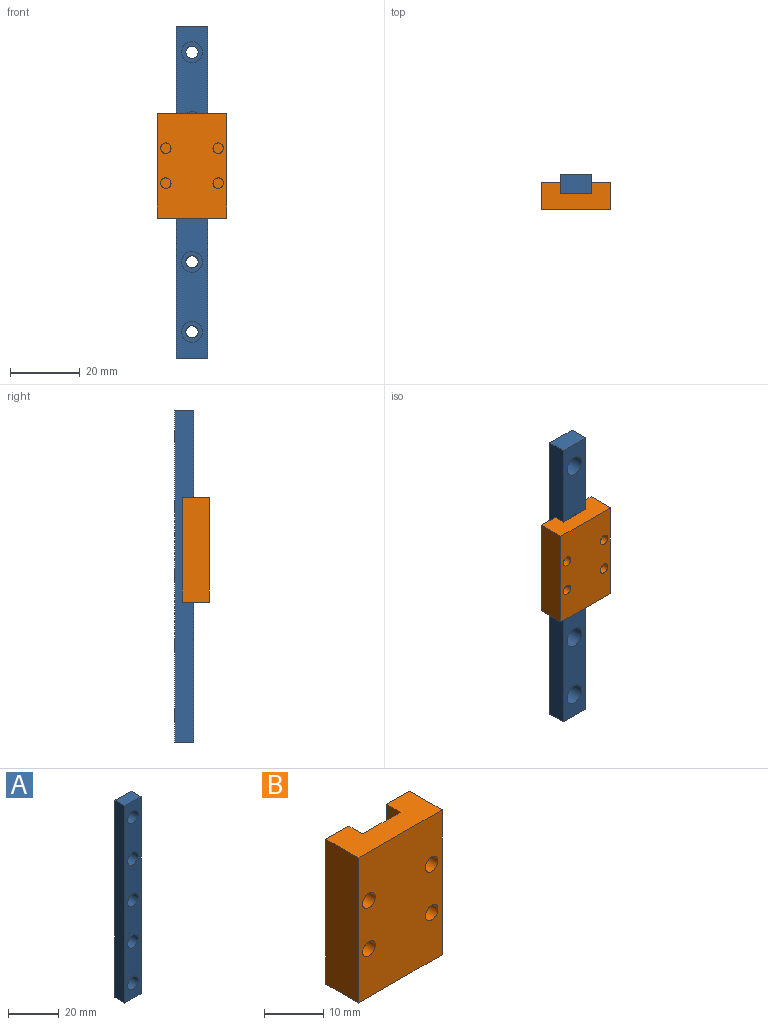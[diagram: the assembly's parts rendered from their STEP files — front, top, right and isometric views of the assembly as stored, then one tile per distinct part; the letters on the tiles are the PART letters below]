
ASSEMBLY  parts=2 mates=1
PART A: 21 faces, bbox 9x5.5x95 mm
  f0: plane 95x5.5mm, normal (-1,0,0), area 522.5mm2, adj f1,f3,f4,f5
  f1: plane 9x5.5mm, normal (0,0,-1), area 49.5mm2, adj f0,f2,f4,f5
  f2: plane 95x5.5mm, normal (1,0,0), area 522.5mm2, adj f1,f3,f4,f5
  f3: plane 9x5.5mm, normal (0,0,1), area 49.5mm2, adj f0,f2,f4,f5
  f4: plane 95x9mm, normal (0,-1,0), area 713.6mm2, adj f0,f1,f2,f3,f11,f13,f15,f17
  f5: plane 95x9mm, normal (0,1,0), area 806.9mm2, adj f0,f1,f2,f3,f6,f7,f8,f9
  f6: cylinder r=1.75mm len=3.5mm, axis (0,-1,0), area 11mm2, adj f5,f20
  f7: cylinder r=1.75mm len=3.5mm, axis (0,-1,0), area 11mm2, adj f5,f18
  f8: cylinder r=1.75mm len=3.5mm, axis (0,-1,0), area 11mm2, adj f5,f16
  f9: cylinder r=1.75mm len=3.5mm, axis (0,-1,0), area 11mm2, adj f5,f14
  f10: cylinder r=1.75mm len=3.5mm, axis (0,-1,0), area 11mm2, adj f5,f12
  f11: cylinder r=3mm len=6mm, axis (0,-1,0), area 84.8mm2, adj f4,f12
  f12: plane 6x6mm, normal (0,-1,0), area 18.7mm2, adj f10,f11
  f13: cylinder r=3mm len=6mm, axis (0,-1,0), area 84.8mm2, adj f4,f14
  f14: plane 6x6mm, normal (0,-1,0), area 18.7mm2, adj f9,f13
  f15: cylinder r=3mm len=6mm, axis (0,-1,0), area 84.8mm2, adj f4,f16
  f16: plane 6x6mm, normal (0,-1,0), area 18.7mm2, adj f8,f15
  f17: cylinder r=3mm len=6mm, axis (0,-1,0), area 84.8mm2, adj f4,f18
  f18: plane 6x6mm, normal (0,-1,0), area 18.7mm2, adj f7,f17
  f19: cylinder r=3mm len=6mm, axis (0,-1,0), area 84.8mm2, adj f4,f20
  f20: plane 6x6mm, normal (0,-1,0), area 18.7mm2, adj f6,f19
PART B: 18 faces, bbox 20x7.8x30 mm
  f0: plane 30x20mm, normal (0,-1,0), area 571.7mm2, adj f2,f3,f4,f5,f10,f12,f14,f16
  f1: plane 30x5.5mm, normal (0,1,0), area 165mm2, adj f2,f3,f5,f9
  f2: plane 20x7.8mm, normal (0,0,-1), area 126.3mm2, adj f0,f1,f4,f5,f6,f7,f8,f9
  f3: plane 20x7.8mm, normal (0,0,1), area 126.3mm2, adj f0,f1,f4,f5,f6,f7,f8,f9
  f4: plane 30x7.8mm, normal (-1,0,0), area 234mm2, adj f0,f2,f3,f6
  f5: plane 30x7.8mm, normal (1,0,0), area 234mm2, adj f0,f1,f2,f3
  f6: plane 30x5.5mm, normal (0,1,0), area 165mm2, adj f2,f3,f4,f8
  f7: plane 30x9mm, normal (0,1,0), area 270mm2, adj f2,f3,f8,f9
  f8: plane 30x3.3mm, normal (1,0,0), area 99mm2, adj f2,f3,f6,f7
  f9: plane 30x3.3mm, normal (-1,0,0), area 99mm2, adj f1,f2,f3,f7
  f10: cylinder r=1.5mm len=3mm, axis (0,-1,0), area 28.3mm2, adj f0,f11
  f11: plane 3x3mm, normal (0,-1,0), area 7.1mm2, adj f10
  f12: cylinder r=1.5mm len=3mm, axis (0,-1,0), area 28.3mm2, adj f0,f13
  f13: plane 3x3mm, normal (0,-1,0), area 7.1mm2, adj f12
  f14: cylinder r=1.5mm len=3mm, axis (0,-1,0), area 28.3mm2, adj f0,f15
  f15: plane 3x3mm, normal (0,-1,0), area 7.1mm2, adj f14
  f16: cylinder r=1.5mm len=3mm, axis (0,-1,0), area 28.3mm2, adj f0,f17
  f17: plane 3x3mm, normal (0,-1,0), area 7.1mm2, adj f16
PLACE A t=(-43.65,-9.51,2.92)mm fixed
PLACE B t=(-43.65,-9.51,7.82)mm
MATE slider B.f3 <-> A.f3  axis (0,0,1) through (-43.65,-15.01,25.45)mm
